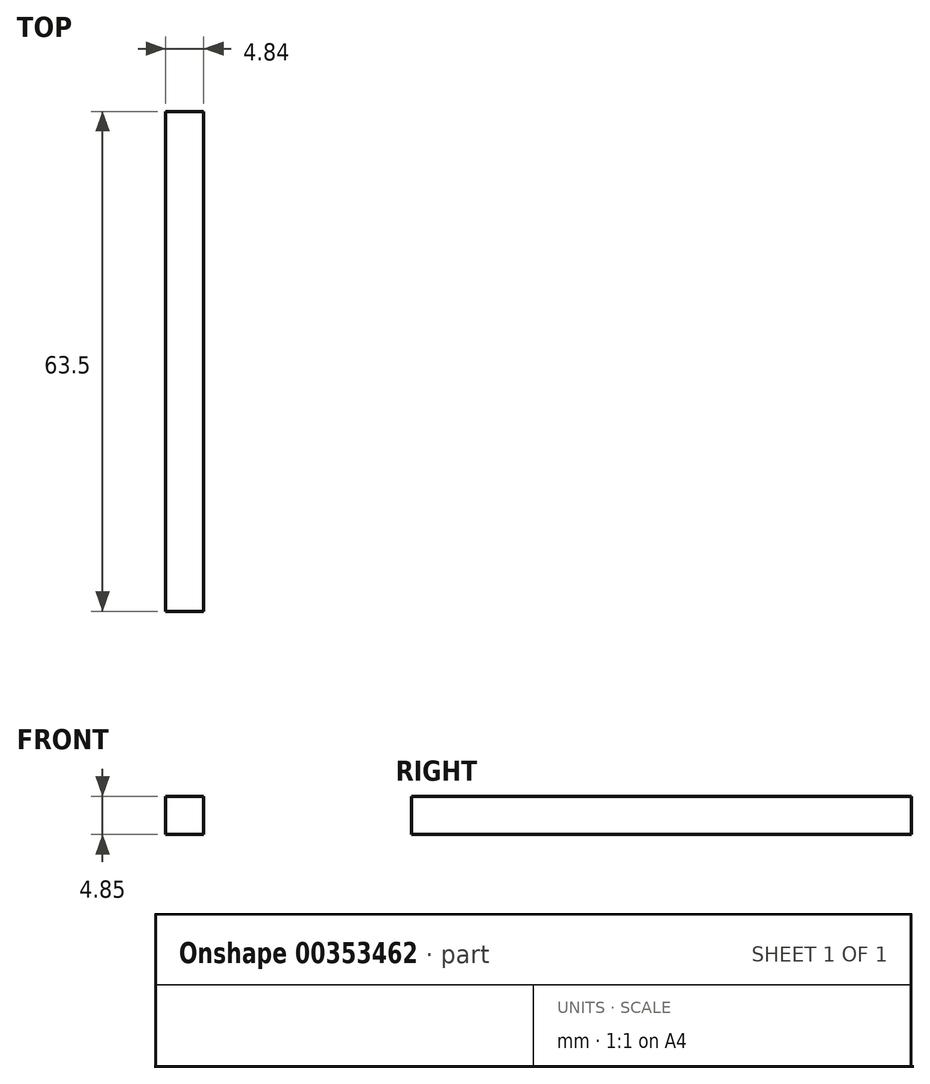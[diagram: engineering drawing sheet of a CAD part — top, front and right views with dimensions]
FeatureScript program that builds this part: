
annotation { "Feature Type Name" : "Feature", "Feature Type Description" : "" }
export const myFeature = defineFeature(function(context is Context, id is Id, definition is map)
    precondition{}
    {
        {
            var Q0;
            Q0=qCreatedBy(makeId("Front.planeOp"),FACE);
            var sketch = newSketch(context, id + "F0", { "sketchPlane" : qUnion([Q0])});
            skLineSegment(sketch, "E0.bottom", {"start": v(-52.48, 63.18) * mm, "end": v(-47.64, 63.18) * mm});
            skLineSegment(sketch, "E0.top", {"start": v(-52.48, 58.33) * mm, "end": v(-47.64, 58.33) * mm});
            skLineSegment(sketch, "E0.left", {"start": v(-52.48, 63.18) * mm, "end": v(-52.48, 58.33) * mm});
            skLineSegment(sketch, "E0.right", {"start": v(-47.64, 63.18) * mm, "end": v(-47.64, 58.33) * mm});
            skSolve(sketch);
        }
        {
            var Q0;
            Q0 = qSketchRegion(id + "F0", true);
            extrude(context, id + "F1", {"entities" : qUnion([Q0]), "depth" : 63.5 * mm});
        }
    });
